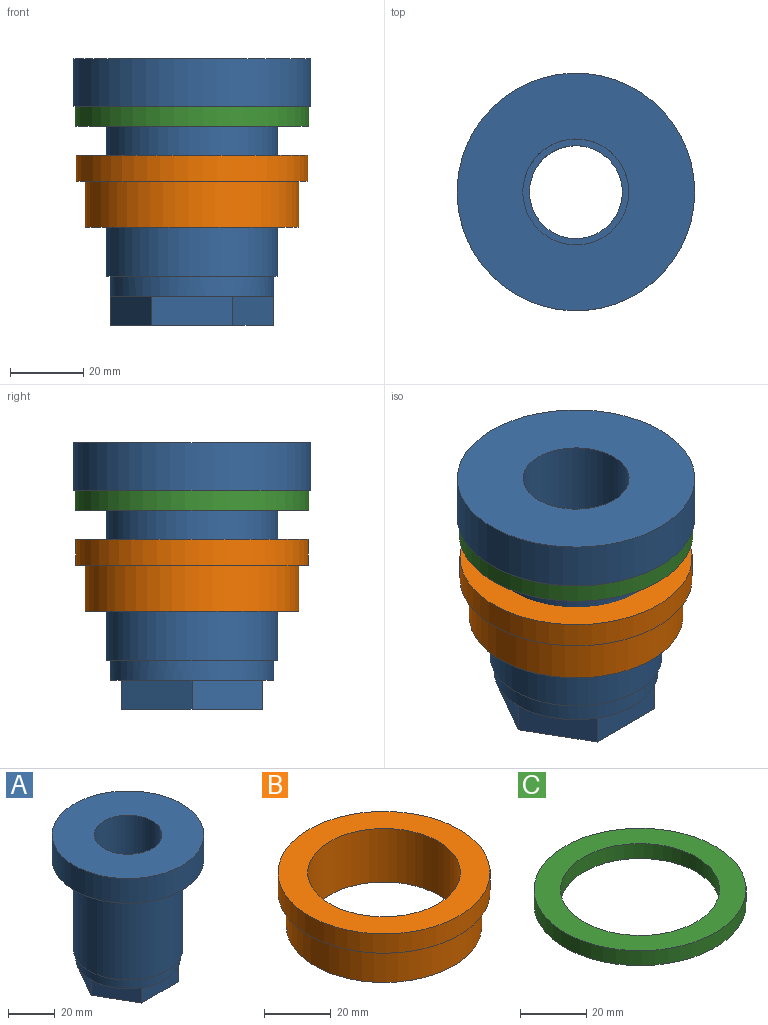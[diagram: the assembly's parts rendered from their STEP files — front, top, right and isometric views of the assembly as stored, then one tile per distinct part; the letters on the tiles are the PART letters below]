
ASSEMBLY  parts=3 mates=2
PART A: 24 faces, bbox 65x65x73 mm
  f0: plane 22.35x2.99mm, normal (0,0,-1), area 45.2mm2, adj f12,f17
  f1: plane 19.36x11.18mm, normal (0,0,-1), area 45.2mm2, adj f12,f22
  f2: plane 19.36x11.18mm, normal (0,0,-1), area 45.2mm2, adj f12,f21
  f3: plane 22.35x2.99mm, normal (0,0,-1), area 45.2mm2, adj f12,f20
  f4: plane 19.36x11.18mm, normal (0,0,-1), area 45.2mm2, adj f12,f19
  f5: plane 19.36x11.18mm, normal (0,0,-1), area 45.2mm2, adj f12,f18
  f6: plane 65x65mm, normal (0,0,1), area 2657.8mm2, adj f7,f16
  f7: cylinder r=14.5mm len=29mm, axis (0,0,1), area 2314.1mm2, adj f6,f8
  f8: plane 29x29mm, normal (0,0,1), area 153.8mm2, adj f7,f9
  f9: cylinder r=12.7mm len=25.4mm, axis (0,0,1), area 1739.6mm2, adj f8,f10
  f10: plane 29x29mm, normal (0,0,-1), area 153.8mm2, adj f9,f11
  f11: cylinder r=14.5mm len=29mm, axis (0,0,1), area 2350.5mm2, adj f10,f23
  f12: cylinder r=22.35mm len=44.7mm, axis (0,0,1), area 758.3mm2, adj f0,f1,f2,f3,f4,f5,f13
  f13: plane 47x47mm, normal (0,0,-1), area 165.6mm2, adj f12,f14
  f14: cylinder r=23.5mm len=47mm, axis (0,0,1), area 6880.7mm2, adj f13,f15
  f15: plane 65x65mm, normal (0,0,-1), area 1583.4mm2, adj f14,f16
  f16: cylinder r=32.5mm len=65mm, axis (0,0,1), area 2654.6mm2, adj f6,f15
  f17: plane 22.35x8mm, normal (0,1,0), area 178.8mm2, adj f0,f18,f22,f23
  f18: plane 19.36x11.18mm, normal (0.87,0.5,0), area 178.8mm2, adj f5,f17,f19,f23
  f19: plane 19.36x11.18mm, normal (0.87,-0.5,0), area 178.8mm2, adj f4,f18,f20,f23
  f20: plane 22.35x8mm, normal (0,-1,0), area 178.8mm2, adj f3,f19,f21,f23
  f21: plane 19.36x11.18mm, normal (-0.87,-0.5,0), area 178.8mm2, adj f2,f20,f22,f23
  f22: plane 19.36x11.18mm, normal (-0.87,0.5,0), area 178.8mm2, adj f1,f17,f21,f23
  f23: plane 44.7x38.71mm, normal (0,0,-1), area 637.3mm2, adj f11,f17,f18,f19,f20,f21,f22
PART B: 6 faces, bbox 63.5x63.5x19.6 mm
  f0: plane 63.5x63.5mm, normal (0,0,1), area 1523mm2, adj f1,f5
  f1: cylinder r=22.88mm len=45.75mm, axis (0,0,1), area 2817.1mm2, adj f0,f2
  f2: plane 58.5x58.5mm, normal (0,0,-1), area 1043.9mm2, adj f1,f3
  f3: cylinder r=29.25mm len=58.5mm, axis (0,0,1), area 2297.3mm2, adj f2,f4
  f4: plane 63.5x63.5mm, normal (0,0,-1), area 479.1mm2, adj f3,f5
  f5: cylinder r=31.75mm len=63.5mm, axis (0,0,1), area 1416.4mm2, adj f0,f4
PART C: 4 faces, bbox 64x64x5.5 mm
  f0: cylinder r=24mm len=48mm, axis (0,0,-1), area 829.4mm2, adj f2,f3
  f1: cylinder r=32mm len=64mm, axis (0,0,-1), area 1105.8mm2, adj f2,f3
  f2: plane 64x64mm, normal (0,0,1), area 1407.4mm2, adj f0,f1
  f3: plane 64x64mm, normal (0,0,-1), area 1407.4mm2, adj f0,f1
PLACE A at identity
PLACE B t=(0,0,10.57)mm
PLACE C at identity
MATE cylindrical B.f1 <-> A.f7  axis (0,0,1) through (0,0,-17.8)mm
MATE fastened A.f7 <-> C.f1  axis (0,0,-1) through (0,0,5.5)mm
